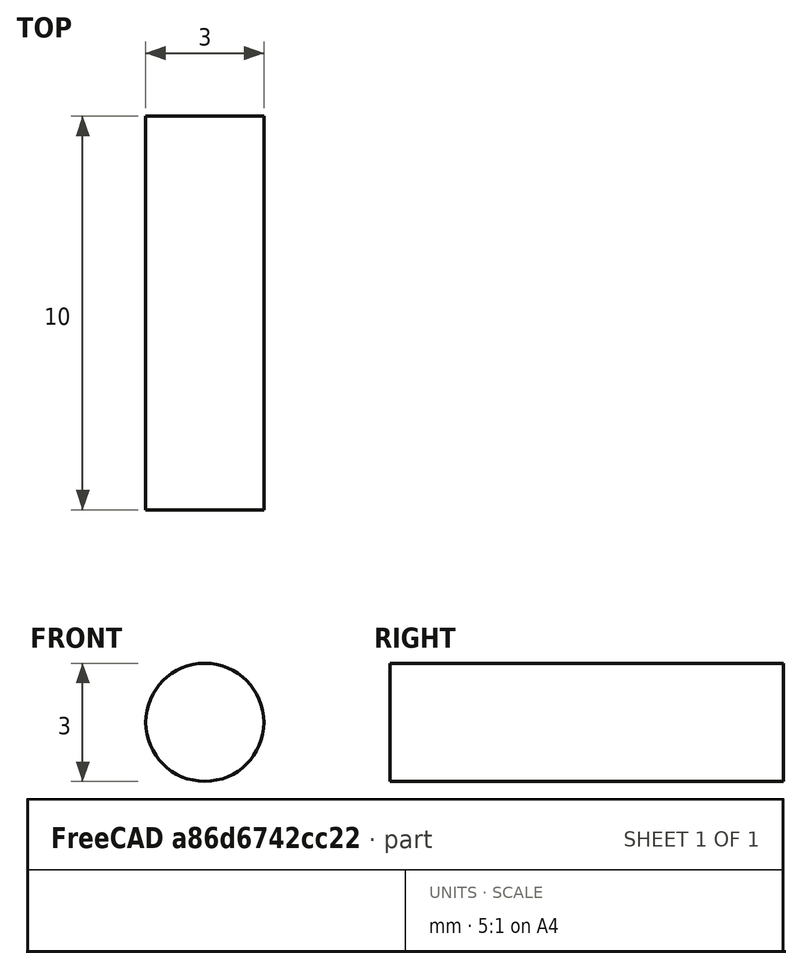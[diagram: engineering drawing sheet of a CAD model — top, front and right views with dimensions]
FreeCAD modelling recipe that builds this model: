
FCSTD DOCUMENT  (FreeCAD 0.19R)
Label: pin_3mmx10mm
License: All rights reserved
LicenseURL: http://en.wikipedia.org/wiki/All_rights_reserved
objects: Sketcher::SketchObject×1, PartDesign::Pad×1, PartDesign::Body×1
note: 4 computed .brp shape members not serialized (recipe doc carries the construction recipe); baked Part::Feature solids carry a one-line shape summary decoded from their .brp

FEATURE [Sketcher::SketchObject] Sketch
  FullyConstrained = true
  MapMode = 5
  Placement = pos=(0,0,0) rot=(1,0,0;1.5708rad)
  Support = -> [XZ_Plane]
  sketch-geometry (1):
    g0: Circle CenterX=0 CenterY=0 CenterZ=0 NormalX=0 NormalY=0 NormalZ=1 AngleXU=0 Radius=1.5
  constraints (2):
    c: Coincident(g0,g-1)
    c: Radius(g0) = 1.5
FEATURE [PartDesign::Pad] Pad
  Direction = (1,1,1)
  Length = 10
  Length2 = 100
  Midplane = true
  Placement = pos=(0,0,0) rot=(1,0,0;1.5708rad)
  Profile = -> Sketch
  Type = 0
FEATURE [PartDesign::Body] Body
  Group = -> [Sketch,Pad]
  Origin = -> Origin
  Tip = -> Pad
